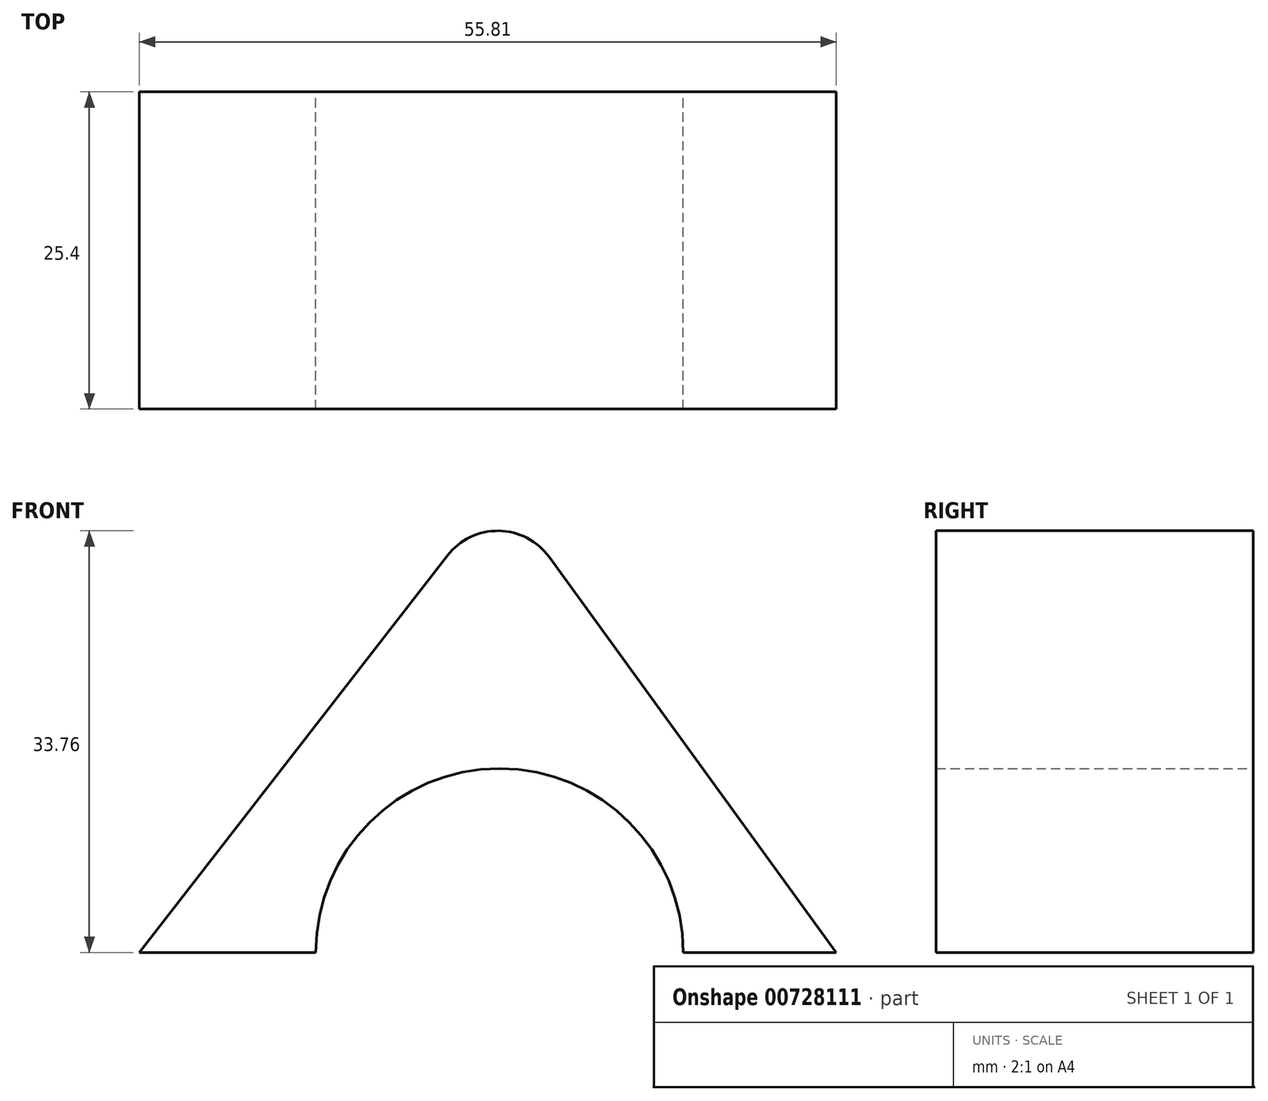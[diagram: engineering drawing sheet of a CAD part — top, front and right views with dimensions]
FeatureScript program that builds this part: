
annotation { "Feature Type Name" : "Feature", "Feature Type Description" : "" }
export const myFeature = defineFeature(function(context is Context, id is Id, definition is map)
    precondition{}
    {
        {
            var Q0;
            Q0=qCreatedBy(makeId("Front.planeOp"),FACE);
            var sketch = newSketch(context, id + "F0", { "sketchPlane" : qUnion([Q0])});
            skLineSegment(sketch, "E0", {"start": v(0, 0) * mm, "end": v(26.97, 0) * mm});
            skLineSegment(sketch, "E1", {"start": v(26.97, 0) * mm, "end": v(0, 37.13) * mm});
            skLineSegment(sketch, "E2", {"start": v(0, 37.13) * mm, "end": v(-28.84, 0) * mm});
            skLineSegment(sketch, "E3", {"start": v(-28.84, 0) * mm, "end": v(0, 0) * mm});
            skSolve(sketch);
        }
        {
            var Q0;
            Q0 = qSketchRegion(id + "F0", true);
            extrude(context, id + "F1", {"entities" : qUnion([Q0]), "endBound" : BoundingType.SYMMETRIC, "depth" : 25.4 * mm, "offsetDistance" : 25.4 * mm});
        }
        {
            var Q0;
            Q0=qCreatedBy(makeId("Front.planeOp"),FACE);
            var sketch = newSketch(context, id + "F2", { "sketchPlane" : qUnion([Q0])});
            skCircle(sketch, "E4", {"center": v(0, 0) * mm, "radius": 14.72 * mm});
            skSolve(sketch);
        }
        {
            var Q0;
            Q0=makeQuery(id+"F2.imprint","IMPRINT",FACE,{"disambiguationData":[TD([[makeQuery(id+"F2.imprint","IMPRINT",EDGE,{"derivedFrom":sQuery(id+"F2.wireOp",EDGE,"E4")}),1.0]])]});
            extrude(context, id + "F3", {"entities" : qUnion([Q0]), "operationType" : NewBodyOperationType.REMOVE, "endBound" : BoundingType.SYMMETRIC, "depth" : 45.2 * mm, "offsetDistance" : 25.4 * mm});
        }
        {
            var Q0;
            Q0=makeQuery(id+"F1.opExtrude","SWEPT_EDGE",EDGE,{"disambiguationData":[OSD([sQuery(id+"F0.wireOp",EDGE,"E1"),sQuery(id+"F0.wireOp",EDGE,"E2")])]});
            fillet(context, id + "F4", {"entities" : qUnion([Q0]), "radius" : 5.08 * mm, "tangentPropagation" : true, "allowEdgeOverflow" : false});
        }
    });
